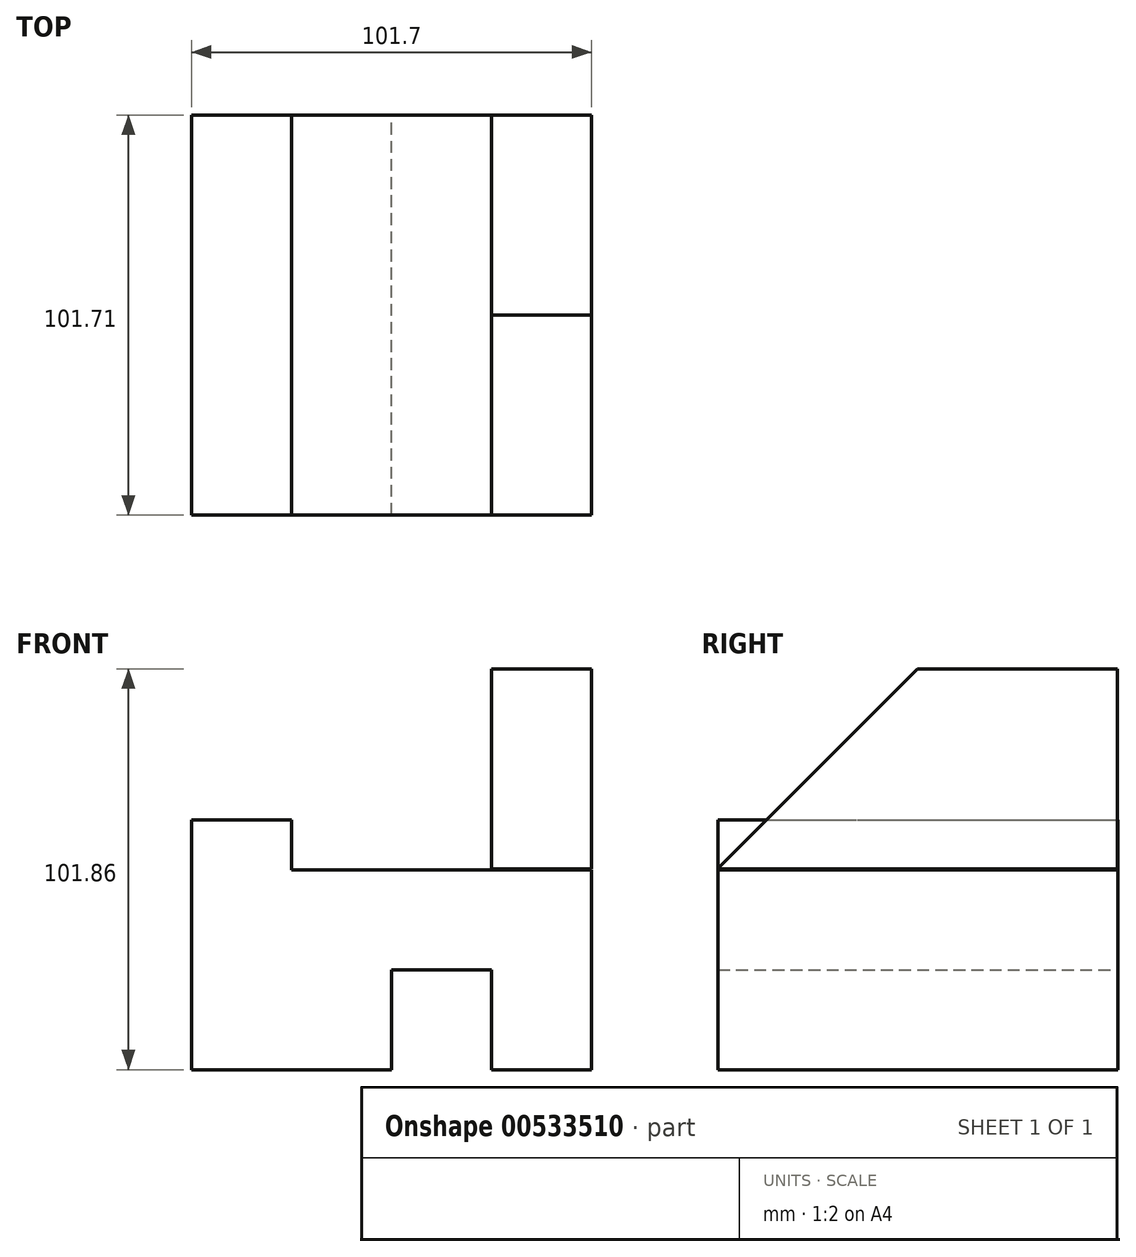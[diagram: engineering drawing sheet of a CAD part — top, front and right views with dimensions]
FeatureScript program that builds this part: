
annotation { "Feature Type Name" : "Feature", "Feature Type Description" : "" }
export const myFeature = defineFeature(function(context is Context, id is Id, definition is map)
    precondition{}
    {
        {
            var Q0;
            Q0=qCreatedBy(makeId("Front.planeOp"),FACE);
            var sketch = newSketch(context, id + "F0", { "sketchPlane" : qUnion([Q0])});
            skLineSegment(sketch, "E0", {"start": v(-45.31, -11) * mm, "end": v(5.49, -11) * mm});
            skLineSegment(sketch, "E1", {"start": v(5.49, -11) * mm, "end": v(5.49, 14.4) * mm});
            skLineSegment(sketch, "E2", {"start": v(5.49, 14.4) * mm, "end": v(30.89, 14.4) * mm});
            skLineSegment(sketch, "E3", {"start": v(30.89, 14.4) * mm, "end": v(30.89, -11) * mm});
            skLineSegment(sketch, "E4", {"start": v(30.89, -11) * mm, "end": v(56.29, -11) * mm});
            skLineSegment(sketch, "E5", {"start": v(-45.31, -11) * mm, "end": v(-45.31, 52.5) * mm});
            skLineSegment(sketch, "E6", {"start": v(-45.31, 52.5) * mm, "end": v(-19.91, 52.5) * mm});
            skLineSegment(sketch, "E7", {"start": v(-19.91, 52.5) * mm, "end": v(-19.91, 39.8) * mm});
            skLineSegment(sketch, "E8", {"start": v(-19.91, 39.8) * mm, "end": v(30.89, 39.8) * mm});
            skLineSegment(sketch, "E9", {"start": v(56.29, -11) * mm, "end": v(56.29, 39.8) * mm});
            skLineSegment(sketch, "E10", {"start": v(56.29, 39.8) * mm, "end": v(30.89, 39.8) * mm});
            skSolve(sketch);
        }
        {
            var Q0;
            Q0=makeQuery(id+"F0.imprint","IMPRINT",FACE,{"disambiguationData":[TD([[makeQuery(id+"F0.imprint","IMPRINT",EDGE,{"derivedFrom":sQuery(id+"F0.wireOp",EDGE,"E0")}),1.0]])]});
            extrude(context, id + "F1", {"entities" : qUnion([Q0]), "depth" : 101.6 * mm, "offsetDistance" : 25.4 * mm});
        }
        {
            var Q0;
            Q0=qCreatedBy(makeId("Right.planeOp"),FACE);
            var sketch = newSketch(context, id + "F2", { "sketchPlane" : qUnion([Q0])});
            skLineSegment(sketch, "E11", {"start": v(-5.7, -64.84) * mm, "end": v(-5.7, -14.04) * mm});
            skLineSegment(sketch, "E12", {"start": v(-5.7, -14.04) * mm, "end": v(-56.5, -14.04) * mm});
            skLineSegment(sketch, "E13", {"start": v(-5.7, -64.84) * mm, "end": v(-107.3, -64.84) * mm});
            skLineSegment(sketch, "E14", {"start": v(-56.5, -14.04) * mm, "end": v(-107.3, -64.84) * mm});
            skSolve(sketch);
        }
        {
            var Q0;
            Q0=makeQuery(id+"F2.imprint","IMPRINT",FACE,{"disambiguationData":[TD([[makeQuery(id+"F2.imprint","IMPRINT",EDGE,{"derivedFrom":sQuery(id+"F2.wireOp",EDGE,"E11")}),1.0]])]});
            extrude(context, id + "F3", {"entities" : qUnion([Q0]), "depth" : 25.4 * mm, "offsetDistance" : 25.4 * mm});
        }
        {
            var Q0;
            Q0=makeQuery(id+"F3.opExtrude","SWEPT_BODY",BODY,{"disambiguationData":[OSD([sQuery(id+"F2.wireOp",EDGE,"E11"),sQuery(id+"F2.wireOp",EDGE,"E12"),sQuery(id+"F2.wireOp",EDGE,"E13"),sQuery(id+"F2.wireOp",EDGE,"E14")])]});
            transform(context, id + "F4", {"entities" : qUnion([Q0]), "transformType" : TransformType.TRANSLATION_3D, "dx" : 30.99 * mm, "dy" : 5.6 * mm, "dz" : 104.9 * mm, "makeCopy" : false});
        }
    });
